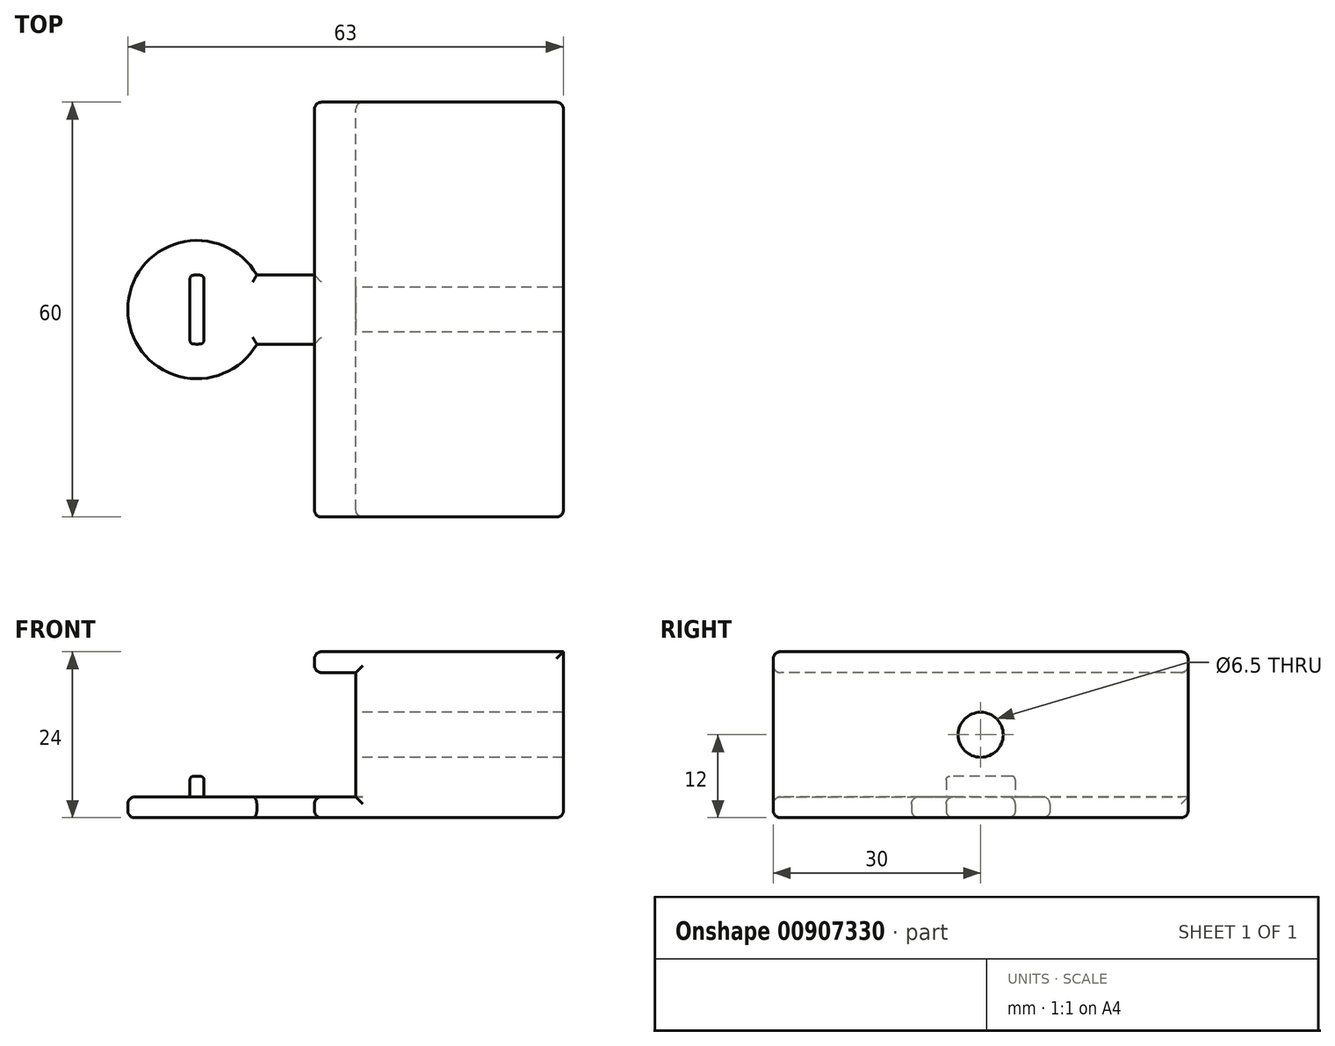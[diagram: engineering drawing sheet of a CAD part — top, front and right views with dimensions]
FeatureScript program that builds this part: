
annotation { "Feature Type Name" : "Feature", "Feature Type Description" : "" }
export const myFeature = defineFeature(function(context is Context, id is Id, definition is map)
    precondition{}
    {
        {
            var Q0;
            Q0=qCreatedBy(makeId("Top.planeOp"),FACE);
            var sketch = newSketch(context, id + "F0", { "sketchPlane" : qUnion([Q0])});
            skCircle(sketch, "E0", {"center": v(0, 0) * mm, "radius": 5 * mm});
            skLineSegment(sketch, "E1.bottom", {"start": v(8.66, 5) * mm, "end": v(17, 5) * mm});
            skLineSegment(sketch, "E1.top", {"start": v(8.66, -5) * mm, "end": v(17, -5) * mm});
            skLineSegment(sketch, "E2.bottom", {"start": v(17, 30) * mm, "end": v(53, 30) * mm});
            skLineSegment(sketch, "E2.top", {"start": v(17, -30) * mm, "end": v(53, -30) * mm});
            skLineSegment(sketch, "E2.left", {"start": v(17, 30) * mm, "end": v(17, 5) * mm});
            skLineSegment(sketch, "E2.right", {"start": v(53, 30) * mm, "end": v(53, -30) * mm});
            skLineSegment(sketch, "E3.trimOffspring", {"start": v(17, -5) * mm, "end": v(17, -30) * mm});
            skArc(sketch, "E4.0", {"start": v(8.66, 5) * mm, "mid": v(-10, 0) * mm, "end": v(8.66, -5) * mm});
            skSolve(sketch);
        }
        {
            var Q0;
            Q0=makeQuery(id+"F0.imprint","IMPRINT",FACE,{"disambiguationData":[TD([[makeQuery(id+"F0.imprint","IMPRINT",EDGE,{"derivedFrom":sQuery(id+"F0.wireOp",EDGE,"E0")}),-1.0]])]});
            var Q1;
            Q1=makeQuery(id+"F0.imprint","IMPRINT",FACE,{"disambiguationData":[TD([[makeQuery(id+"F0.imprint","IMPRINT",EDGE,{"derivedFrom":sQuery(id+"F0.wireOp",EDGE,"E0")}),1.0]])]});
            extrude(context, id + "F1", {"entities" : qUnion([Q0, Q1]), "depth" : 3 * mm, "offsetDistance" : 25 * mm});
        }
        {
            var Q0;
            Q0=makeQuery(id+"F1.opExtrude","CAP_FACE",FACE,{"disambiguationData":[OSD([sQuery(id+"F0.wireOp",EDGE,"E1.bottom"),sQuery(id+"F0.wireOp",EDGE,"E1.top"),sQuery(id+"F0.wireOp",EDGE,"E2.bottom"),sQuery(id+"F0.wireOp",EDGE,"E2.top"),sQuery(id+"F0.wireOp",EDGE,"E2.left"),sQuery(id+"F0.wireOp",EDGE,"E2.right"),sQuery(id+"F0.wireOp",EDGE,"E3.trimOffspring"),sQuery(id+"F0.wireOp",EDGE,"E4.0")])],"isStart":false});
            var sketch = newSketch(context, id + "F2", { "sketchPlane" : qUnion([Q0])});
            skArc(sketch, "E5", {"start": v(1, 4.9) * mm, "mid": v(0, 5) * mm, "end": v(-1, 4.9) * mm});
            skLineSegment(sketch, "E6.left", {"start": v(-1, 4.9) * mm, "end": v(-1, -4.9) * mm});
            skLineSegment(sketch, "E6.right", {"start": v(1, 4.9) * mm, "end": v(1, -4.9) * mm});
            skArc(sketch, "E7.trimOffspring", {"start": v(-1, -4.9) * mm, "mid": v(0, -5) * mm, "end": v(1, -4.9) * mm});
            skSolve(sketch);
        }
        {
            var Q0;
            Q0=makeQuery(id+"F2.imprint","IMPRINT",FACE,{"disambiguationData":[TD([[makeQuery(id+"F2.imprint","IMPRINT",EDGE,{"derivedFrom":sQuery(id+"F2.wireOp",EDGE,"E5")}),1.0]])]});
            extrude(context, id + "F3", {"entities" : qUnion([Q0]), "operationType" : NewBodyOperationType.ADD, "depth" : 3 * mm, "offsetDistance" : 25 * mm});
        }
        {
            var Q0;
            Q0=makeQuery(id+"F1.opExtrude","CAP_FACE",FACE,{"disambiguationData":[OSD([sQuery(id+"F0.wireOp",EDGE,"E1.bottom"),sQuery(id+"F0.wireOp",EDGE,"E1.top"),sQuery(id+"F0.wireOp",EDGE,"E2.bottom"),sQuery(id+"F0.wireOp",EDGE,"E2.top"),sQuery(id+"F0.wireOp",EDGE,"E2.left"),sQuery(id+"F0.wireOp",EDGE,"E2.right"),sQuery(id+"F0.wireOp",EDGE,"E3.trimOffspring"),sQuery(id+"F0.wireOp",EDGE,"E4.0")])],"isStart":false});
            var sketch = newSketch(context, id + "F4", { "sketchPlane" : qUnion([Q0])});
            skLineSegment(sketch, "E8.bottom", {"start": v(53, -30) * mm, "end": v(23, -30) * mm});
            skLineSegment(sketch, "E8.top", {"start": v(53, 30) * mm, "end": v(23, 30) * mm});
            skLineSegment(sketch, "E8.left", {"start": v(53, -30) * mm, "end": v(53, 30) * mm});
            skLineSegment(sketch, "E8.right", {"start": v(23, -30) * mm, "end": v(23, 30) * mm});
            skSolve(sketch);
        }
        {
            var Q0;
            Q0=makeQuery(id+"F4.imprint","IMPRINT",FACE,{"disambiguationData":[TD([[makeQuery(id+"F4.imprint","IMPRINT",EDGE,{"derivedFrom":sQuery(id+"F4.wireOp",EDGE,"E8.bottom")}),1.0]])]});
            extrude(context, id + "F5", {"entities" : qUnion([Q0]), "operationType" : NewBodyOperationType.ADD, "depth" : 21 * mm, "offsetDistance" : 25 * mm});
        }
        {
            var Q0;
            Q0=makeQuery(id+"F5.opExtrude","SWEPT_FACE",FACE,{"disambiguationData":[OSD([sQuery(id+"F4.wireOp",EDGE,"E8.right")])]});
            var sketch = newSketch(context, id + "F6", { "sketchPlane" : qUnion([Q0])});
            skLineSegment(sketch, "E9.bottom", {"start": v(-30, 24) * mm, "end": v(30, 24) * mm});
            skLineSegment(sketch, "E9.top", {"start": v(-30, 21) * mm, "end": v(30, 21) * mm});
            skLineSegment(sketch, "E9.left", {"start": v(-30, 24) * mm, "end": v(-30, 21) * mm});
            skLineSegment(sketch, "E9.right", {"start": v(30, 24) * mm, "end": v(30, 21) * mm});
            skSolve(sketch);
        }
        {
            var Q0;
            Q0=makeQuery(id+"F6.imprint","IMPRINT",FACE,{"disambiguationData":[TD([[makeQuery(id+"F6.imprint","IMPRINT",EDGE,{"derivedFrom":sQuery(id+"F6.wireOp",EDGE,"fWSQJ5K4-b7GI-DkJu-ht6W-kSiYVOIKomN2.bottom")}),1.0]])]});
            var Q1;
            Q1=makeQuery(id+"F6.imprint","IMPRINT",FACE,{"disambiguationData":[TD([[makeQuery(id+"F6.imprint","IMPRINT",EDGE,{"derivedFrom":sQuery(id+"F6.wireOp",EDGE,"E9.bottom")}),1.0]])]});
            extrude(context, id + "F7", {"entities" : qUnion([Q0, Q1]), "operationType" : NewBodyOperationType.ADD, "depth" : 6 * mm, "offsetDistance" : 25 * mm});
        }
        {
            var Q0;
            Q0=makeQuery(id+"F5.opExtrude","SWEPT_FACE",FACE,{"disambiguationData":[OSD([sQuery(id+"F4.wireOp",EDGE,"E8.right")])]});
            var sketch = newSketch(context, id + "F8", { "sketchPlane" : qUnion([Q0])});
            skCircle(sketch, "E10", {"center": v(0, 12) * mm, "radius": 3.25 * mm});
            skSolve(sketch);
        }
        {
            var Q0;
            Q0=makeQuery(id+"F8.imprint","IMPRINT",FACE,{"disambiguationData":[TD([[makeQuery(id+"F8.imprint","IMPRINT",EDGE,{"derivedFrom":sQuery(id+"F8.wireOp",EDGE,"E10")}),1.0]])]});
            extrude(context, id + "F9", {"entities" : qUnion([Q0]), "operationType" : NewBodyOperationType.REMOVE, "oppositeDirection" : true, "depth" : 30 * mm, "offsetDistance" : 25 * mm});
        }
        {
            var Q0;
            Q0=makeQuery(id+"F7.opExtrude","CAP_EDGE",EDGE,{"disambiguationData":[OSD([sQuery(id+"F6.wireOp",EDGE,"fWSQJ5K4-b7GI-DkJu-ht6W-kSiYVOIKomN2.top")])],"isStart":false});
            var Q1;
            Q1=makeQuery(id+"F7.opExtrude","SWEPT_EDGE",EDGE,{"disambiguationData":[OSD([sQuery(id+"F6.wireOp",EDGE,"fWSQJ5K4-b7GI-DkJu-ht6W-kSiYVOIKomN2.top"),sQuery(id+"F6.wireOp",EDGE,"fWSQJ5K4-b7GI-DkJu-ht6W-kSiYVOIKomN2.right")])]});
            var Q2;
            Q2=makeQuery(id+"F7.opExtrude","SWEPT_EDGE",EDGE,{"disambiguationData":[OSD([sQuery(id+"F6.wireOp",EDGE,"fWSQJ5K4-b7GI-DkJu-ht6W-kSiYVOIKomN2.top"),sQuery(id+"F6.wireOp",EDGE,"fWSQJ5K4-b7GI-DkJu-ht6W-kSiYVOIKomN2.left")])]});
            var Q3;
            Q3=makeQuery(id+"F7.opExtrude","CAP_EDGE",EDGE,{"disambiguationData":[OSD([sQuery(id+"F6.wireOp",EDGE,"fWSQJ5K4-b7GI-DkJu-ht6W-kSiYVOIKomN2.bottom")])],"isStart":false});
            var Q4;
            Q4=makeQuery(id+"F5.boolean.opBoolean","MERGE",EDGE,{"derivedFrom":[makeQuery(id+"F1.opExtrude","SWEPT_EDGE",EDGE,{"disambiguationData":[OSD([sQuery(id+"F0.wireOp",EDGE,"E2.top"),sQuery(id+"F0.wireOp",EDGE,"E3.trimOffspring")])]}),makeQuery(id+"F5.opExtrude","SWEPT_EDGE",EDGE,{"disambiguationData":[OSD([sQuery(id+"F4.wireOp",EDGE,"MdE1tAoH-8TG7-EFZc-bhcy-uvtnGmuwVBnL.bottom"),sQuery(id+"F4.wireOp",EDGE,"MdE1tAoH-8TG7-EFZc-bhcy-uvtnGmuwVBnL.right")])]})]});
            var Q5;
            Q5=makeQuery(id+"F5.boolean.opBoolean","MERGE",EDGE,{"derivedFrom":[makeQuery(id+"F1.opExtrude","SWEPT_EDGE",EDGE,{"disambiguationData":[OSD([sQuery(id+"F0.wireOp",EDGE,"E2.bottom"),sQuery(id+"F0.wireOp",EDGE,"E2.left")])]}),makeQuery(id+"F5.opExtrude","SWEPT_EDGE",EDGE,{"disambiguationData":[OSD([sQuery(id+"F4.wireOp",EDGE,"MdE1tAoH-8TG7-EFZc-bhcy-uvtnGmuwVBnL.top"),sQuery(id+"F4.wireOp",EDGE,"MdE1tAoH-8TG7-EFZc-bhcy-uvtnGmuwVBnL.right")])]})]});
            var Q6;
            Q6=makeQuery(id+"F9.boolean.opBoolean","COPY",EDGE,{"derivedFrom":makeQuery(id+"F9.opExtrude","CAP_EDGE",EDGE,{"disambiguationData":[OSD([sQuery(id+"F8.wireOp",EDGE,"E10")])],"isStart":true})});
            var Q7;
            Q7=makeQuery(id+"F1.opExtrude","CAP_EDGE",EDGE,{"disambiguationData":[OSD([sQuery(id+"F0.wireOp",EDGE,"E1.top")])],"isStart":false});
            var Q8;
            Q8=makeQuery(id+"F1.opExtrude","CAP_EDGE",EDGE,{"disambiguationData":[OSD([sQuery(id+"F0.wireOp",EDGE,"E4.0")])],"isStart":false});
            var Q9;
            Q9=makeQuery(id+"F1.opExtrude","CAP_EDGE",EDGE,{"disambiguationData":[OSD([sQuery(id+"F0.wireOp",EDGE,"E1.bottom")])],"isStart":false});
            var Q10;
            {var subQ0=sQuery(id+"F4.wireOp",EDGE,"MdE1tAoH-8TG7-EFZc-bhcy-uvtnGmuwVBnL.right");Q10=makeQuery(id+"F7.boolean.opBoolean","SPLIT",EDGE,{"disambiguationData":[TD([makeQuery(id+"F1.opExtrude","SWEPT_FACE",FACE,{"disambiguationData":[OSD([sQuery(id+"F0.wireOp",EDGE,"E2.bottom")])]})])],"derivedFrom":makeQuery(id+"F5.opExtrude","CAP_EDGE",EDGE,{"disambiguationData":[OSD([subQ0])],"isStart":false})});}
            var Q11;
            Q11=makeQuery(id+"F7.opExtrude","SWEPT_EDGE",EDGE,{"disambiguationData":[OSD([sQuery(id+"F4.wireOp",EDGE,"MdE1tAoH-8TG7-EFZc-bhcy-uvtnGmuwVBnL.right"),sQuery(id+"F6.wireOp",EDGE,"fWSQJ5K4-b7GI-DkJu-ht6W-kSiYVOIKomN2.bottom"),sQuery(id+"F6.wireOp",EDGE,"fWSQJ5K4-b7GI-DkJu-ht6W-kSiYVOIKomN2.left")])]});
            var Q12;
            Q12=makeQuery(id+"F7.opExtrude","SWEPT_EDGE",EDGE,{"disambiguationData":[OSD([sQuery(id+"F4.wireOp",EDGE,"MdE1tAoH-8TG7-EFZc-bhcy-uvtnGmuwVBnL.right"),sQuery(id+"F6.wireOp",EDGE,"fWSQJ5K4-b7GI-DkJu-ht6W-kSiYVOIKomN2.bottom"),sQuery(id+"F6.wireOp",EDGE,"fWSQJ5K4-b7GI-DkJu-ht6W-kSiYVOIKomN2.right")])]});
            var Q13;
            {var subQ1=sQuery(id+"F4.wireOp",EDGE,"MdE1tAoH-8TG7-EFZc-bhcy-uvtnGmuwVBnL.right");Q13=makeQuery(id+"F7.boolean.opBoolean","SPLIT",EDGE,{"disambiguationData":[TD([makeQuery(id+"F1.opExtrude","SWEPT_FACE",FACE,{"disambiguationData":[OSD([sQuery(id+"F0.wireOp",EDGE,"E2.top")])]})])],"derivedFrom":makeQuery(id+"F5.opExtrude","CAP_EDGE",EDGE,{"disambiguationData":[OSD([subQ1])],"isStart":false})});}
            var Q14;
            Q14=makeQuery(id+"F5.opExtrude","CAP_EDGE",EDGE,{"disambiguationData":[OSD([sQuery(id+"F4.wireOp",EDGE,"MdE1tAoH-8TG7-EFZc-bhcy-uvtnGmuwVBnL.bottom")])],"isStart":false});
            var Q15;
            Q15=makeQuery(id+"F5.opExtrude","CAP_EDGE",EDGE,{"disambiguationData":[OSD([sQuery(id+"F4.wireOp",EDGE,"MdE1tAoH-8TG7-EFZc-bhcy-uvtnGmuwVBnL.left")])],"isStart":false});
            var Q16;
            Q16=makeQuery(id+"F1.opExtrude","CAP_EDGE",EDGE,{"disambiguationData":[OSD([sQuery(id+"F0.wireOp",EDGE,"E2.bottom")])],"isStart":true});
            var Q17;
            Q17=makeQuery(id+"F5.boolean.opBoolean","MERGE",EDGE,{"derivedFrom":[makeQuery(id+"F1.opExtrude","SWEPT_EDGE",EDGE,{"disambiguationData":[OSD([sQuery(id+"F0.wireOp",EDGE,"E2.bottom"),sQuery(id+"F0.wireOp",EDGE,"E2.right")])]}),makeQuery(id+"F5.opExtrude","SWEPT_EDGE",EDGE,{"disambiguationData":[OSD([sQuery(id+"F4.wireOp",EDGE,"MdE1tAoH-8TG7-EFZc-bhcy-uvtnGmuwVBnL.top"),sQuery(id+"F4.wireOp",EDGE,"MdE1tAoH-8TG7-EFZc-bhcy-uvtnGmuwVBnL.left")])]})]});
            var Q18;
            Q18=makeQuery(id+"F1.opExtrude","CAP_EDGE",EDGE,{"disambiguationData":[OSD([sQuery(id+"F0.wireOp",EDGE,"E2.left")])],"isStart":true});
            var Q19;
            Q19=makeQuery(id+"F1.opExtrude","CAP_EDGE",EDGE,{"disambiguationData":[OSD([sQuery(id+"F0.wireOp",EDGE,"E1.bottom")])],"isStart":true});
            var Q20;
            Q20=makeQuery(id+"F1.opExtrude","CAP_EDGE",EDGE,{"disambiguationData":[OSD([sQuery(id+"F0.wireOp",EDGE,"E4.0")])],"isStart":true});
            var Q21;
            Q21=makeQuery(id+"F1.opExtrude","CAP_EDGE",EDGE,{"disambiguationData":[OSD([sQuery(id+"F0.wireOp",EDGE,"E1.top")])],"isStart":true});
            var Q22;
            Q22=makeQuery(id+"F1.opExtrude","CAP_EDGE",EDGE,{"disambiguationData":[OSD([sQuery(id+"F0.wireOp",EDGE,"E3.trimOffspring")])],"isStart":true});
            var Q23;
            Q23=makeQuery(id+"F1.opExtrude","CAP_EDGE",EDGE,{"disambiguationData":[OSD([sQuery(id+"F0.wireOp",EDGE,"E2.right")])],"isStart":true});
            var Q24;
            Q24=makeQuery(id+"F1.opExtrude","CAP_EDGE",EDGE,{"disambiguationData":[OSD([sQuery(id+"F0.wireOp",EDGE,"E2.top")])],"isStart":true});
            var Q25;
            Q25=makeQuery(id+"F5.boolean.opBoolean","MERGE",EDGE,{"derivedFrom":[makeQuery(id+"F1.opExtrude","SWEPT_EDGE",EDGE,{"disambiguationData":[OSD([sQuery(id+"F0.wireOp",EDGE,"E2.top"),sQuery(id+"F0.wireOp",EDGE,"E2.right")])]}),makeQuery(id+"F5.opExtrude","SWEPT_EDGE",EDGE,{"disambiguationData":[OSD([sQuery(id+"F4.wireOp",EDGE,"MdE1tAoH-8TG7-EFZc-bhcy-uvtnGmuwVBnL.bottom"),sQuery(id+"F4.wireOp",EDGE,"MdE1tAoH-8TG7-EFZc-bhcy-uvtnGmuwVBnL.left")])]})]});
            var Q26;
            Q26=makeQuery(id+"F9.boolean.opBoolean","COPY",EDGE,{"derivedFrom":makeQuery(id+"F9.opExtrude","CAP_EDGE",EDGE,{"disambiguationData":[OSD([sQuery(id+"F8.wireOp",EDGE,"E10")])],"isStart":false})});
            var Q27;
            Q27=makeQuery(id+"F7.opExtrude","CAP_EDGE",EDGE,{"disambiguationData":[OSD([sQuery(id+"F6.wireOp",EDGE,"fWSQJ5K4-b7GI-DkJu-ht6W-kSiYVOIKomN2.right")])],"isStart":false});
            var Q28;
            Q28=makeQuery(id+"F7.opExtrude","CAP_EDGE",EDGE,{"disambiguationData":[OSD([sQuery(id+"F6.wireOp",EDGE,"fWSQJ5K4-b7GI-DkJu-ht6W-kSiYVOIKomN2.left")])],"isStart":false});
            var Q29;
            Q29=makeQuery(id+"F5.opExtrude","SWEPT_EDGE",EDGE,{"disambiguationData":[OSD([sQuery(id+"F0.wireOp",EDGE,"E2.top"),sQuery(id+"F4.wireOp",EDGE,"E8.bottom"),sQuery(id+"F4.wireOp",EDGE,"E8.right")])]});
            var Q30;
            Q30=makeQuery(id+"F5.opExtrude","SWEPT_EDGE",EDGE,{"disambiguationData":[OSD([sQuery(id+"F0.wireOp",EDGE,"E2.bottom"),sQuery(id+"F4.wireOp",EDGE,"E8.top"),sQuery(id+"F4.wireOp",EDGE,"E8.right")])]});
            var Q31;
            Q31=makeQuery(id+"F7.opExtrude","SWEPT_EDGE",EDGE,{"disambiguationData":[OSD([sQuery(id+"F0.wireOp",EDGE,"E2.bottom"),sQuery(id+"F4.wireOp",EDGE,"E8.top"),sQuery(id+"F4.wireOp",EDGE,"E8.right"),sQuery(id+"F6.wireOp",EDGE,"E9.top"),sQuery(id+"F6.wireOp",EDGE,"E9.left")])]});
            var Q32;
            Q32=makeQuery(id+"F7.opExtrude","CAP_EDGE",EDGE,{"disambiguationData":[OSD([sQuery(id+"F6.wireOp",EDGE,"E9.top")])],"isStart":false});
            var Q33;
            Q33=makeQuery(id+"F7.opExtrude","CAP_EDGE",EDGE,{"disambiguationData":[OSD([sQuery(id+"F6.wireOp",EDGE,"E9.left")])],"isStart":false});
            var Q34;
            Q34=makeQuery(id+"F7.opExtrude","CAP_EDGE",EDGE,{"disambiguationData":[OSD([sQuery(id+"F6.wireOp",EDGE,"E9.bottom")])],"isStart":false});
            var Q35;
            Q35=makeQuery(id+"F7.boolean.opBoolean","MERGE",EDGE,{"derivedFrom":[makeQuery(id+"F5.opExtrude","CAP_EDGE",EDGE,{"disambiguationData":[OSD([sQuery(id+"F4.wireOp",EDGE,"E8.top")])],"isStart":false}),makeQuery(id+"F7.opExtrude","SWEPT_EDGE",EDGE,{"disambiguationData":[OSD([sQuery(id+"F6.wireOp",EDGE,"E9.bottom"),sQuery(id+"F6.wireOp",EDGE,"E9.left")])]})]});
            var Q36;
            Q36=makeQuery(id+"F7.boolean.opBoolean","MERGE",EDGE,{"derivedFrom":[makeQuery(id+"F5.opExtrude","CAP_EDGE",EDGE,{"disambiguationData":[OSD([sQuery(id+"F4.wireOp",EDGE,"E8.bottom")])],"isStart":false}),makeQuery(id+"F7.opExtrude","SWEPT_EDGE",EDGE,{"disambiguationData":[OSD([sQuery(id+"F6.wireOp",EDGE,"E9.bottom"),sQuery(id+"F6.wireOp",EDGE,"E9.right")])]})]});
            var Q37;
            Q37=makeQuery(id+"F7.opExtrude","CAP_EDGE",EDGE,{"disambiguationData":[OSD([sQuery(id+"F6.wireOp",EDGE,"E9.right")])],"isStart":false});
            var Q38;
            Q38=makeQuery(id+"F7.opExtrude","SWEPT_EDGE",EDGE,{"disambiguationData":[OSD([sQuery(id+"F0.wireOp",EDGE,"E2.top"),sQuery(id+"F4.wireOp",EDGE,"E8.bottom"),sQuery(id+"F4.wireOp",EDGE,"E8.right"),sQuery(id+"F6.wireOp",EDGE,"E9.top"),sQuery(id+"F6.wireOp",EDGE,"E9.right")])]});
            var Q39;
            Q39=makeQuery(id+"F1.opExtrude","CAP_EDGE",EDGE,{"disambiguationData":[OSD([sQuery(id+"F0.wireOp",EDGE,"E2.top")])],"isStart":false});
            var Q40;
            Q40=makeQuery(id+"F1.opExtrude","CAP_EDGE",EDGE,{"disambiguationData":[OSD([sQuery(id+"F0.wireOp",EDGE,"E3.trimOffspring")])],"isStart":false});
            var Q41;
            Q41=makeQuery(id+"F1.opExtrude","CAP_EDGE",EDGE,{"disambiguationData":[OSD([sQuery(id+"F0.wireOp",EDGE,"E2.left")])],"isStart":false});
            var Q42;
            Q42=makeQuery(id+"F1.opExtrude","SWEPT_EDGE",EDGE,{"disambiguationData":[OSD([sQuery(id+"F0.wireOp",EDGE,"E2.top"),sQuery(id+"F0.wireOp",EDGE,"E3.trimOffspring")])]});
            var Q43;
            Q43=makeQuery(id+"F1.opExtrude","SWEPT_EDGE",EDGE,{"disambiguationData":[OSD([sQuery(id+"F0.wireOp",EDGE,"E2.bottom"),sQuery(id+"F0.wireOp",EDGE,"E2.left")])]});
            fillet(context, id + "F10", {"entities" : qUnion([Q0, Q1, Q2, Q3, Q4, Q5, Q6, Q7, Q8, Q9, Q10, Q11, Q12, Q13, Q14, Q15, Q16, Q17, Q18, Q19, Q20, Q21, Q22, Q23, Q24, Q25, Q26, Q27, Q28, Q29, Q30, Q31, Q32, Q33, Q34, Q35, Q36, Q37, Q38, Q39, Q40, Q41, Q42, Q43]), "radius" : 1 * mm, "tangentPropagation" : true, "allowEdgeOverflow" : false});
        }
        {
            var Q0;
            Q0=makeQuery(id+"F3.opExtrude","CAP_EDGE",EDGE,{"disambiguationData":[OSD([sQuery(id+"F2.wireOp",EDGE,"E7.trimOffspring")])],"isStart":false});
            var Q1;
            Q1=makeQuery(id+"F3.opExtrude","CAP_EDGE",EDGE,{"disambiguationData":[OSD([sQuery(id+"F2.wireOp",EDGE,"E5")])],"isStart":false});
            var Q2;
            Q2=makeQuery(id+"F3.opExtrude","SWEPT_EDGE",EDGE,{"disambiguationData":[OSD([sQuery(id+"F2.wireOp",EDGE,"E6.left"),sQuery(id+"F2.wireOp",EDGE,"E7.trimOffspring")])]});
            var Q3;
            Q3=makeQuery(id+"F3.opExtrude","SWEPT_EDGE",EDGE,{"disambiguationData":[OSD([sQuery(id+"F2.wireOp",EDGE,"E6.right"),sQuery(id+"F2.wireOp",EDGE,"E7.trimOffspring")])]});
            var Q4;
            Q4=makeQuery(id+"F3.opExtrude","SWEPT_EDGE",EDGE,{"disambiguationData":[OSD([sQuery(id+"F2.wireOp",EDGE,"E5"),sQuery(id+"F2.wireOp",EDGE,"E6.right")])]});
            var Q5;
            Q5=makeQuery(id+"F3.opExtrude","SWEPT_EDGE",EDGE,{"disambiguationData":[OSD([sQuery(id+"F2.wireOp",EDGE,"E5"),sQuery(id+"F2.wireOp",EDGE,"E6.left")])]});
            var Q6;
            Q6=makeQuery(id+"F3.opExtrude","CAP_EDGE",EDGE,{"disambiguationData":[OSD([sQuery(id+"F2.wireOp",EDGE,"E6.left")])],"isStart":false});
            var Q7;
            Q7=makeQuery(id+"F3.opExtrude","CAP_EDGE",EDGE,{"disambiguationData":[OSD([sQuery(id+"F2.wireOp",EDGE,"E6.right")])],"isStart":false});
            fillet(context, id + "F11", {"entities" : qUnion([Q0, Q1, Q2, Q3, Q4, Q5, Q6, Q7]), "radius" : 0.5 * mm, "tangentPropagation" : true, "allowEdgeOverflow" : false});
        }
    });
